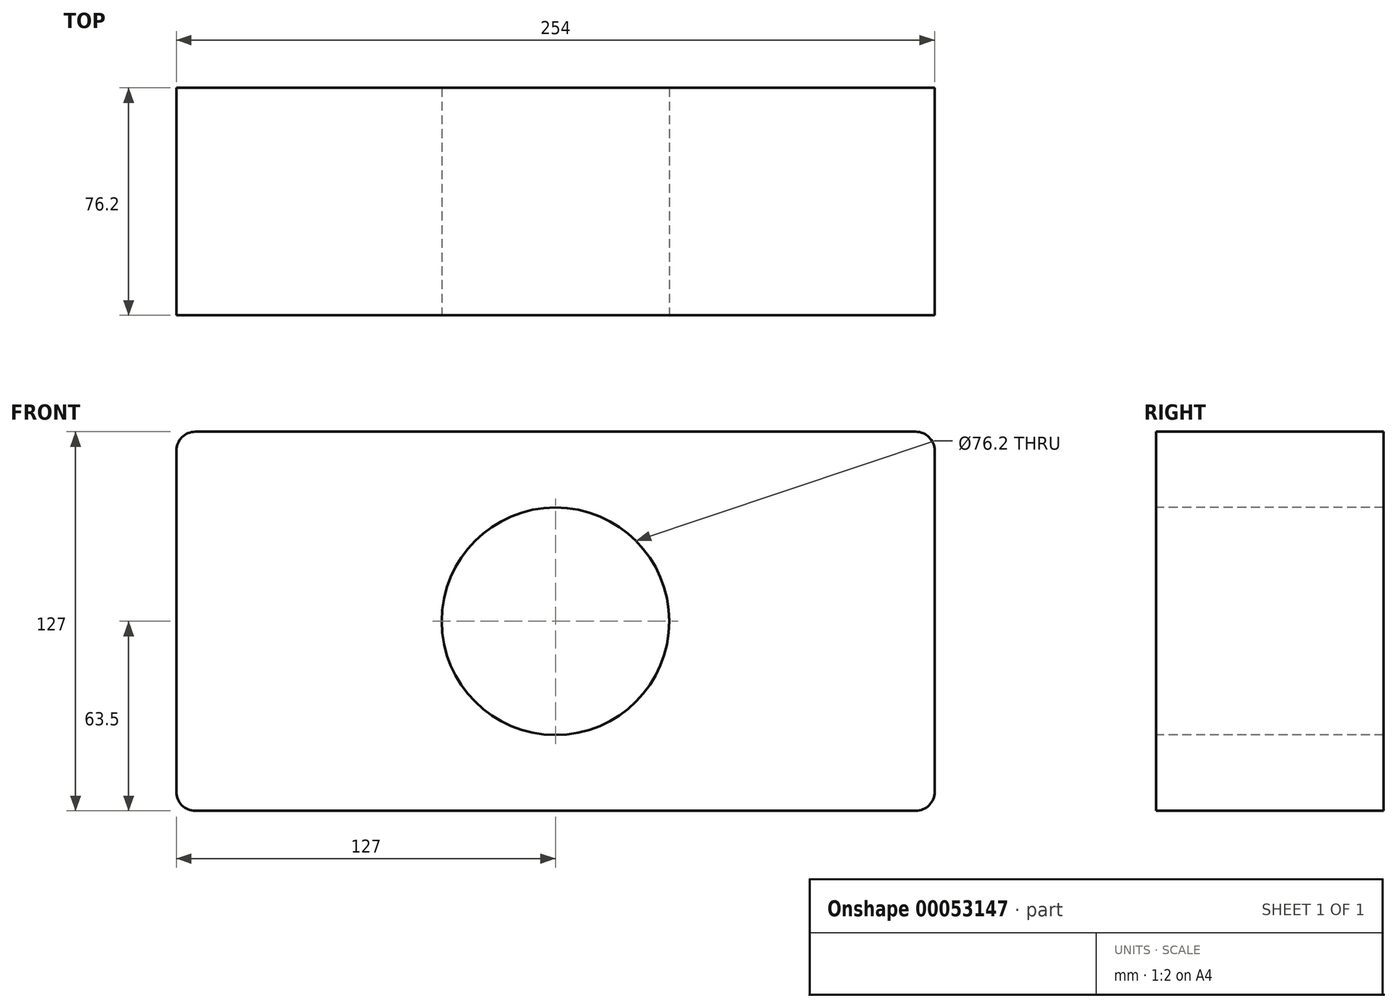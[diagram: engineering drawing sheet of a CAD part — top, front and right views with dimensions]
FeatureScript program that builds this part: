
annotation { "Feature Type Name" : "Feature", "Feature Type Description" : "" }
export const myFeature = defineFeature(function(context is Context, id is Id, definition is map)
    precondition{}
    {
        {
            var Q0;
            Q0=qCreatedBy(makeId("Front.planeOp"),FACE);
            var sketch = newSketch(context, id + "F0", { "sketchPlane" : qUnion([Q0])});
            skLineSegment(sketch, "E0.bottom", {"start": v(-127, 63.5) * mm, "end": v(127, 63.5) * mm});
            skLineSegment(sketch, "E0.top", {"start": v(-127, -63.5) * mm, "end": v(127, -63.5) * mm});
            skLineSegment(sketch, "E0.left", {"start": v(-127, 63.5) * mm, "end": v(-127, -63.5) * mm});
            skLineSegment(sketch, "E0.right", {"start": v(127, 63.5) * mm, "end": v(127, -63.5) * mm});
            skLineSegment(sketch, "E1", {"start": v(-127, 63.5) * mm, "end": v(127, -63.5) * mm, "construction": true});
            skSolve(sketch);
        }
        {
            var Q0;
            Q0=makeQuery(id+"F0.imprint","IMPRINT",FACE,{"disambiguationData":[TD([[makeQuery(id+"F0.imprint","IMPRINT",EDGE,{"derivedFrom":sQuery(id+"F0.wireOp",EDGE,"E0.bottom")}),-1.0]])]});
            extrude(context, id + "F1", {"entities" : qUnion([Q0]), "endBound" : BoundingType.SYMMETRIC, "depth" : 76.2 * mm});
        }
        {
            var Q0;
            Q0=makeQuery(id+"F1.opExtrude","SWEPT_EDGE",EDGE,{"disambiguationData":[OSD([sQuery(id+"F0.wireOp",EDGE,"E0.bottom"),sQuery(id+"F0.wireOp",EDGE,"E0.left")])]});
            var Q1;
            Q1=makeQuery(id+"F1.opExtrude","SWEPT_EDGE",EDGE,{"disambiguationData":[OSD([sQuery(id+"F0.wireOp",EDGE,"E0.bottom"),sQuery(id+"F0.wireOp",EDGE,"E0.right")])]});
            var Q2;
            Q2=makeQuery(id+"F1.opExtrude","SWEPT_EDGE",EDGE,{"disambiguationData":[OSD([sQuery(id+"F0.wireOp",EDGE,"E0.top"),sQuery(id+"F0.wireOp",EDGE,"E0.left")])]});
            var Q3;
            Q3=makeQuery(id+"F1.opExtrude","SWEPT_EDGE",EDGE,{"disambiguationData":[OSD([sQuery(id+"F0.wireOp",EDGE,"E0.top"),sQuery(id+"F0.wireOp",EDGE,"E0.right")])]});
            fillet(context, id + "F2", {"entities" : qUnion([Q0, Q1, Q2, Q3]), "radius" : 6.35 * mm, "tangentPropagation" : true, "allowEdgeOverflow" : false});
        }
        {
            var Q0;
            Q0=makeQuery(id+"F1.opExtrude","CAP_FACE",FACE,{"disambiguationData":[OSD([sQuery(id+"F0.wireOp",EDGE,"E0.bottom"),sQuery(id+"F0.wireOp",EDGE,"E0.top"),sQuery(id+"F0.wireOp",EDGE,"E0.left"),sQuery(id+"F0.wireOp",EDGE,"E0.right")])],"isStart":false});
            var sketch = newSketch(context, id + "F3", { "sketchPlane" : qUnion([Q0])});
            skCircle(sketch, "E2", {"center": v(0, 0) * mm, "radius": 38.1 * mm});
            skSolve(sketch);
        }
        {
            var Q0;
            Q0 = qSketchRegion(id + "F3", true);
            extrude(context, id + "F4", {"entities" : qUnion([Q0]), "operationType" : NewBodyOperationType.REMOVE, "endBound" : BoundingType.THROUGH_ALL, "oppositeDirection" : true, "depth" : 25.4 * mm});
        }
    });
